SOLIDWORKS PART (.sldprt)
format: sldprt  version: not decoded by parser v0  size: 162,816 bytes
history: native  units: mm
features: extrude x7, plane x3, material x1, sketch x1, fillet x1 (+8 scaffold rows collapsed)
feature tree (21):
  scaffold x8  (default folders/planes/origin — collapsed)
  material  "Matériau <non spécifié>"
  plane  "Face"
  plane  "Dessus"
  plane  "Droite"
  sketch  "Esquisse1"
  extrude  "Base-Extrusion"  Depth=0.9mm
  extrude  "Esquisse2"  Depth=0.15mm
  extrude  "Boss.-Extru.1"  Depth=0.5mm
  extrude  "Esquisse3"  [1 undecoded]
  extrude  "Boss.-Extru.2"  Depth=6mm
  extrude  "Esquisse4"  Depth=4.348335mm
  extrude  "Boss.-Extru.3"  Depth=0.2mm
  fillet  "Congé1"  Radius=0.45mm
decode coverage: 7 of 9 modeling features carry decoded parameters
note: 1 parameter value undecoded
note: suppression state not decoded; provenance and decode notes live in map.json
